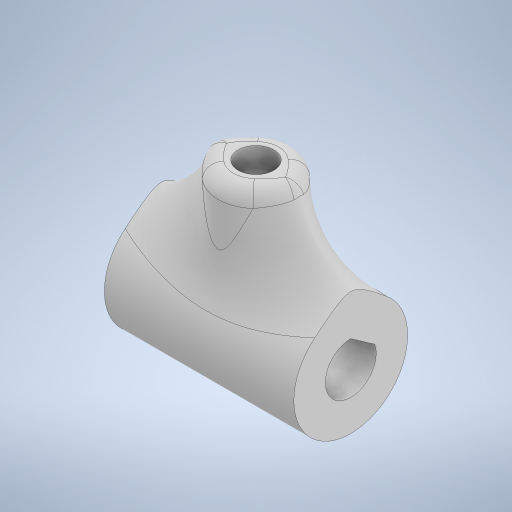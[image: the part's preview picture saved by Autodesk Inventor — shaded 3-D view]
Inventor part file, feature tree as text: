
AUTODESK INVENTOR PART (.ipt)
format: ipt  version: 2024.1 (Build 281209000, 209)  size: 434,176 bytes
history: native  units: mm
features: extrude x8, sketch x8, fillet x2, other x1
ambient origin geometry x8: Origin, YZ Plane, XZ Plane, XY Plane, X Axis, Y Axis, Z Axis, Center Point
bodies: Body1 (feature_tree)
feature tree (19):
  other  "Sólido1"
  extrude  "Extrusão1"  Depth=3.0mm
  extrude  "Extrusão2"  Depth=2.0mm TaperAngle=0.0deg
  extrude  "Extrusão3"  Depth=13.0mm TaperAngle=0.0deg
  extrude  "Extrusão4"  Depth=5.0mm
  extrude  "Extrusão5"  Depth=13.0mm TaperAngle=0.0deg
  extrude  "Extrusão6"  Depth=10.0mm TaperAngle=0.0deg
  extrude  "Extrusão7"  Depth=10.0mm TaperAngle=0.0deg
  extrude  "Extrusão8"  Depth=2.0mm
  fillet  "Arredondamento1"  [1 undecoded]
  fillet  "Arredondamento2"  [1 undecoded]
  sketch  "Esboço2"  dims[d1=15.0mm d2=3.0mm]
  sketch  "Esboço3"  dims[d3=10.0mm d4=0.0mm d5=2.0mm d6=0.0mm]
  sketch  "Esboço4"  dims[d7=6.7mm d8=13.0mm d9=0.0mm]
  sketch  "Esboço5"  dims[d10=13.0mm d11=0.0mm d12=5.0mm]
  sketch  "Esboço6"  dims[d13=10.0mm d14=13.0mm d15=0.0mm]
  sketch  "Esboço7"  dims[d16=4.7mm d17=10.0mm d18=0.0mm]
  sketch  "Esboço8"  dims[d19=10.0mm d20=0.0mm d21=10.0mm d22=0.0mm]
  sketch  "Esboço9"  dims[d23=13.0mm d24=2.0mm]
note: 2 required parameter values undecoded (feature->parameter linkage not recoverable at this tier; creation-order binding heuristic only, values carry confidence <= 0.55)
